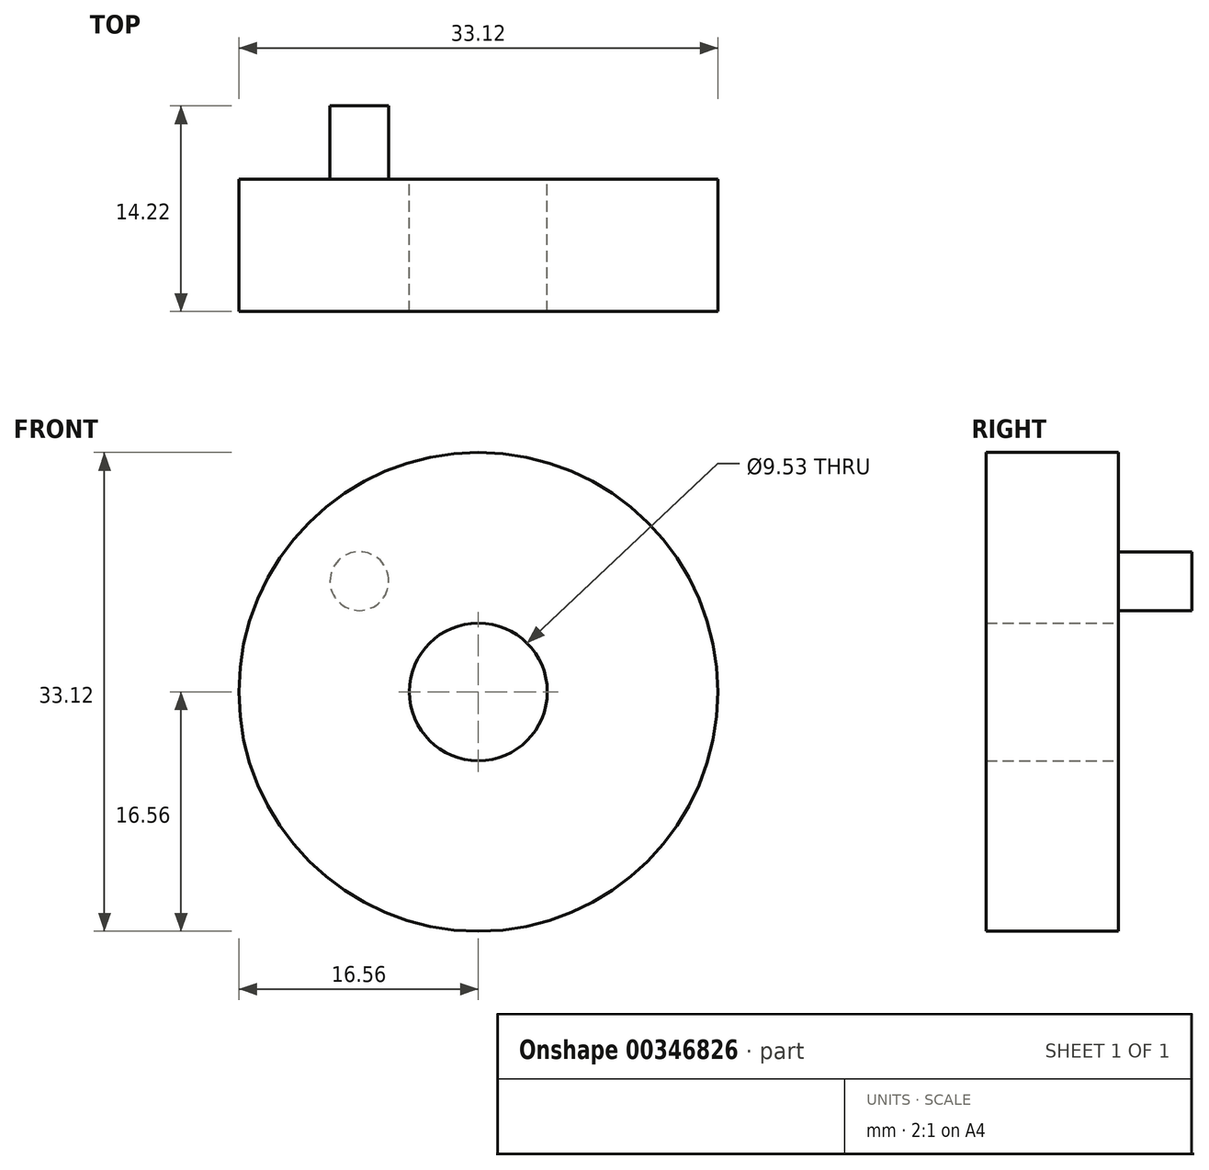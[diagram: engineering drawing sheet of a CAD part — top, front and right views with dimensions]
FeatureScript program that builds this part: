
annotation { "Feature Type Name" : "Feature", "Feature Type Description" : "" }
export const myFeature = defineFeature(function(context is Context, id is Id, definition is map)
    precondition{}
    {
        {
            var Q0;
            Q0=qCreatedBy(makeId("Front.planeOp"),FACE);
            var sketch = newSketch(context, id + "F0", { "sketchPlane" : qUnion([Q0])});
            skCircle(sketch, "E0", {"center": v(0, 0) * mm, "radius": 4.76 * mm});
            skCircle(sketch, "E1", {"center": v(-8.22, 7.66) * mm, "radius": 2.03 * mm});
            skCircle(sketch, "E2", {"center": v(0, 0) * mm, "radius": 16.56 * mm});
            skSolve(sketch);
        }
        {
            var Q0;
            Q0=makeQuery(id+"F0.imprint","IMPRINT",FACE,{"disambiguationData":[TD([[makeQuery(id+"F0.imprint","IMPRINT",EDGE,{"derivedFrom":sQuery(id+"F0.wireOp",EDGE,"E0")}),-1.0]])]});
            var Q1;
            Q1=makeQuery(id+"F0.imprint","IMPRINT",FACE,{"disambiguationData":[TD([[makeQuery(id+"F0.imprint","IMPRINT",EDGE,{"derivedFrom":sQuery(id+"F0.wireOp",EDGE,"E0")}),1.0]])]});
            var Q2;
            Q2=makeQuery(id+"F0.imprint","IMPRINT",FACE,{"disambiguationData":[TD([[makeQuery(id+"F0.imprint","IMPRINT",EDGE,{"derivedFrom":sQuery(id+"F0.wireOp",EDGE,"E1")}),1.0]])]});
            extrude(context, id + "F1", {"entities" : qUnion([Q0, Q1, Q2]), "depth" : 9.14 * mm});
        }
        {
            var Q0;
            Q0=makeQuery(id+"F0.imprint","IMPRINT",FACE,{"disambiguationData":[TD([[makeQuery(id+"F0.imprint","IMPRINT",EDGE,{"derivedFrom":sQuery(id+"F0.wireOp",EDGE,"E1")}),1.0]])]});
            extrude(context, id + "F2", {"entities" : qUnion([Q0]), "operationType" : NewBodyOperationType.ADD, "oppositeDirection" : true, "depth" : 5.08 * mm});
        }
        {
            var Q0;
            Q0=makeQuery(id+"F0.imprint","IMPRINT",FACE,{"disambiguationData":[TD([[makeQuery(id+"F0.imprint","IMPRINT",EDGE,{"derivedFrom":sQuery(id+"F0.wireOp",EDGE,"E0")}),1.0]])]});
            extrude(context, id + "F3", {"entities" : qUnion([Q0]), "operationType" : NewBodyOperationType.REMOVE, "depth" : 24.64 * mm});
        }
    });
